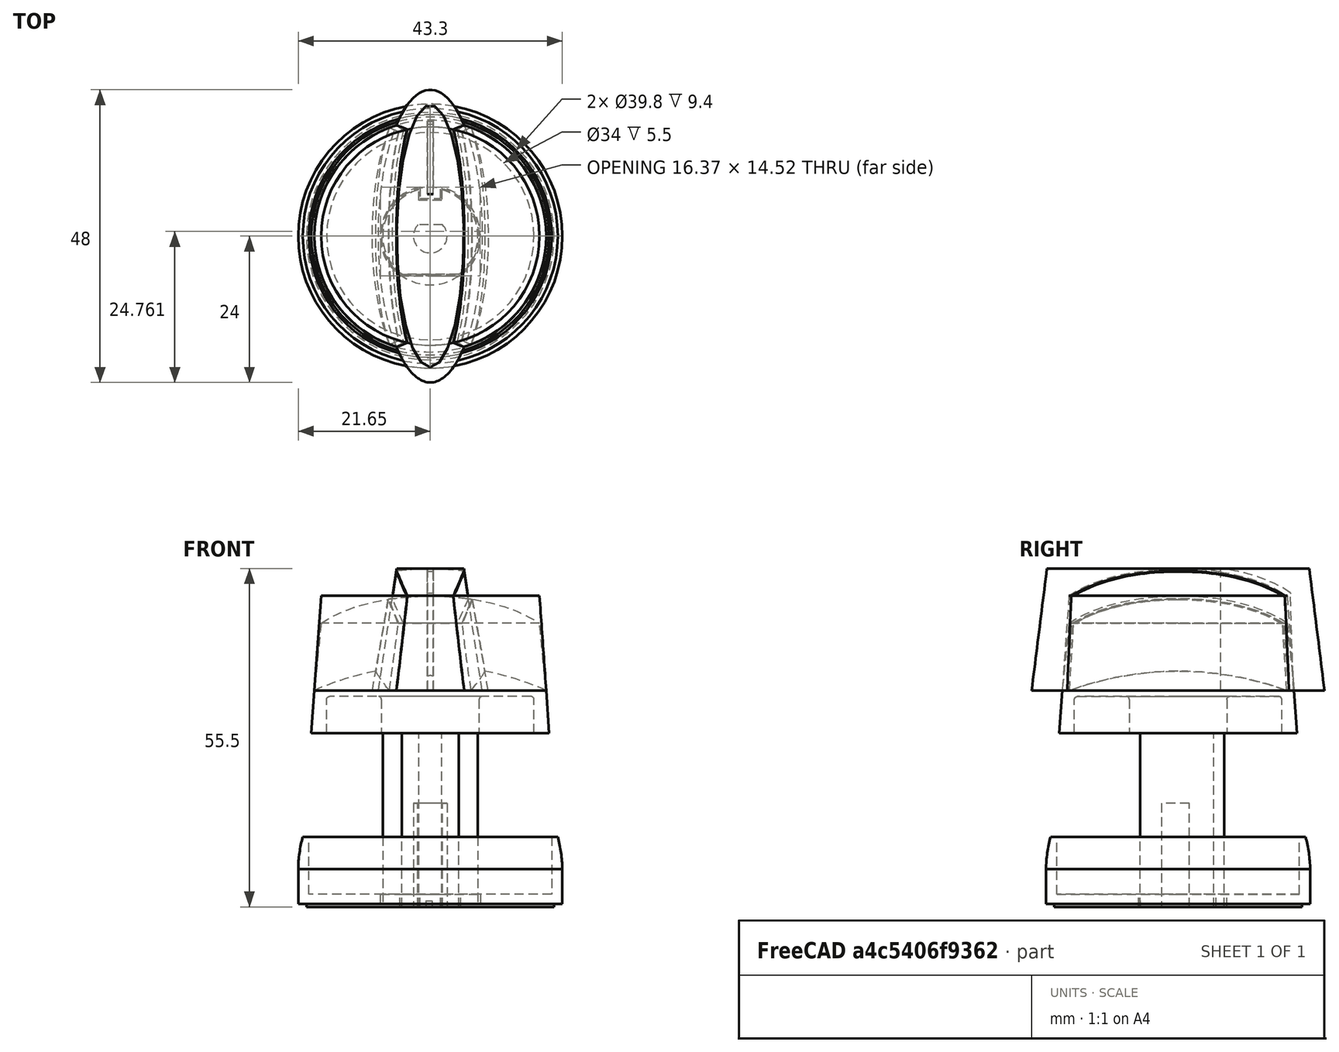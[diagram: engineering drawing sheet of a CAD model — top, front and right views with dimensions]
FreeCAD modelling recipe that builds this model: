
FCSTD DOCUMENT  (FreeCAD 0.18.4R)
Label: electrolux_ruchki_001
License: All rights reserved
LicenseURL: http://en.wikipedia.org/wiki/All_rights_reserved
objects: Sketcher::SketchObject×27, PartDesign::Body×9, PartDesign::Boolean×8, PartDesign::Fillet×8, PartDesign::AdditiveLoft×4, PartDesign::Pad×3, PartDesign::Pocket×3, PartDesign::Revolution×3, PartDesign::Plane×2, PartDesign::Groove×1, App::DocumentObjectGroup×1, PartDesign::AdditiveBox×1, Mesh::Feature×1
note: 84 computed .brp shape members not serialized (recipe doc carries the construction recipe); baked Part::Feature solids carry a one-line shape summary decoded from their .brp

FEATURE [Sketcher::SketchObject] Sketch
  sketch-geometry (8):
    g0: Circle CenterX=0 CenterY=0 CenterZ=0 NormalX=0 NormalY=0 NormalZ=1 AngleXU=0 Radius=21.65
    g1: ArcOfCircle CenterX=0 CenterY=0 CenterZ=0 NormalX=0 NormalY=0 NormalZ=1 AngleXU=0 Radius=8 StartAngle=5.37644 EndAngle=7.63345
    g2: LineSegment StartX=-1.75 StartY=6 StartZ=0 EndX=1.75 EndY=6 EndZ=0
    g3: LineSegment StartX=1.75 StartY=6 StartZ=0 EndX=1.75 EndY=7.80625 EndZ=0
    g4: LineSegment StartX=-1.75 StartY=7.80625 StartZ=0 EndX=-1.75 EndY=6 EndZ=0
    g5: GeomPoint X=0 Y=8 Z=0
    g6: LineSegment StartX=-4.93052 StartY=-6.3 StartZ=0 EndX=4.93052 EndY=-6.3 EndZ=0
    g7: ArcOfCircle CenterX=0 CenterY=0 CenterZ=0 NormalX=0 NormalY=0 NormalZ=1 AngleXU=0 Radius=8 StartAngle=1.79133 EndAngle=4.04833
  constraints (22):
    c: Coincident(g0,g-1)
    c: Radius(g0) = 21.65
    c: Coincident(g0,g1)
    c: Radius(g1) = 8
    c: Coincident(g2,g3)
    c: Coincident(g4,g2)
    c: Vertical(g3)
    c: Vertical(g4)
    c: PointOnObject(g5,g1)
    c: PointOnObject(g5,g-2)
    c: Horizontal(g6)
    c: DistanceY(g6,g2) = 12.3
    c: Coincident(g1,g6)
    c: Coincident(g7,g6)
    c: Coincident(g6,g7)
    c: Coincident(g7,g4)
    c: Coincident(g1,g7)
    c: Coincident(g1,g3)
    c: DistanceX(g2,g2) = 3.5
    c: Equal(g7,g1)
    c: Symmetric(g2,g2,g-2)
    c: DistanceY(g2,g5) = 2
FEATURE [Sketcher::SketchObject] CopySketch  label="основание"
  sketch-geometry (8):
    g0: Circle CenterX=0 CenterY=0 CenterZ=0 NormalX=0 NormalY=0 NormalZ=1 AngleXU=0 Radius=21.65
    g1: ArcOfCircle CenterX=0 CenterY=0 CenterZ=0 NormalX=0 NormalY=0 NormalZ=1 AngleXU=0 Radius=8.2 StartAngle=5.36799 EndAngle=7.64515
    g2: LineSegment StartX=-1.7 StartY=6.2 StartZ=0 EndX=1.7 EndY=6.2 EndZ=0
    g3: LineSegment StartX=1.7 StartY=6.2 StartZ=0 EndX=1.7 EndY=8.02185 EndZ=0
    g4: LineSegment StartX=-1.7 StartY=8.02185 StartZ=0 EndX=-1.7 EndY=6.2 EndZ=0
    g5: GeomPoint X=0 Y=8.2 Z=0
    g6: LineSegment StartX=-4.999 StartY=-6.5 StartZ=0 EndX=4.999 EndY=-6.5 EndZ=0
    g7: ArcOfCircle CenterX=0 CenterY=0 CenterZ=0 NormalX=0 NormalY=0 NormalZ=1 AngleXU=0 Radius=8.2 StartAngle=1.77963 EndAngle=4.05679
  constraints (22):
    c: Coincident(g0,g-1)
    c: Radius(g0) = 21.65
    c: Coincident(g0,g1)
    c: Radius(g1) = 8.2
    c: Coincident(g2,g3)
    c: Coincident(g4,g2)
    c: Vertical(g3)
    c: Vertical(g4)
    c: PointOnObject(g5,g1)
    c: PointOnObject(g5,g-2)
    c: Horizontal(g6)
    c: DistanceY(g6,g2) = 12.7
    c: Coincident(g1,g6)
    c: Coincident(g7,g6)
    c: Coincident(g6,g7)
    c: Coincident(g7,g4)
    c: Coincident(g1,g7)
    c: Coincident(g1,g3)
    c: DistanceX(g2,g2) = 3.4
    c: Equal(g7,g1)
    c: Symmetric(g2,g2,g-2)
    c: DistanceY(g2,g5) = 2
FEATURE [Sketcher::SketchObject] CopySketch001  label="карман2"
  Placement = pos=(0,0,0) rot=(1,0,0;3.14159rad)
  sketch-geometry (2):
    g0: Circle CenterX=0 CenterY=0 CenterZ=0 NormalX=0 NormalY=0 NormalZ=1 AngleXU=0 Radius=21.65
    g1: Circle CenterX=0 CenterY=0 CenterZ=0 NormalX=0 NormalY=0 NormalZ=1 AngleXU=0 Radius=20.3
  constraints (4):
    c: Radius(g1) = 20.3
    c: Radius(g0) = 21.65
    c: Coincident(g1,g-1)
    c: Coincident(g0,g1)
FEATURE [PartDesign::Pad] Pad
  Length = 11.5
  Length2 = 100
  Profile = -> CopySketch
  Type = 0
FEATURE [Sketcher::SketchObject] Sketch002  label="карман"
  MapMode = 5
  Placement = pos=(0,0,11.5) rot=(0,0,1;0rad)
  Support = -> [Pad]
  sketch-geometry (1):
    g0: Circle CenterX=0 CenterY=0 CenterZ=0 NormalX=0 NormalY=0 NormalZ=1 AngleXU=0 Radius=19.9
  constraints (2):
    c: Coincident(g0,g-1)
    c: Radius(g0) = 19.9
FEATURE [PartDesign::Pocket] Pocket
  BaseFeature = -> Pad
  Length = 9.4
  Length2 = 100
  Profile = -> Sketch002
  Type = 0
FEATURE [Sketcher::SketchObject] Sketch003
  MapMode = 5
  Placement = pos=(0,0,11.5) rot=(0,0,1;0rad)
  Support = -> [Pocket]
  sketch-geometry (1):
    g0: Circle CenterX=0 CenterY=0 CenterZ=0 NormalX=0 NormalY=0 NormalZ=1 AngleXU=0 Radius=20.5
  constraints (2):
    c: Coincident(g0,g-1)
    c: Radius(g0) = 20.5
FEATURE [PartDesign::Pocket] Pocket001
  BaseFeature = -> Pocket
  Length = 0.5
  Length2 = 100
  Profile = -> CopySketch001
  Type = 0
FEATURE [Sketcher::SketchObject] Sketch004  label="скругление"
  ExternalGeometry = -> [Pad]
  MapMode = 5
  Placement = pos=(0,0,0) rot=(1,0,0;1.5708rad)
  Support = -> [XZ_Plane]
  sketch-geometry (3):
    g0: LineSegment StartX=21.65 StartY=6.5 StartZ=0 EndX=21.65 EndY=11.5 EndZ=0
    g1: LineSegment StartX=20.9 StartY=11.5 StartZ=0 EndX=21.65 EndY=11.5 EndZ=0
    g2: ArcOfCircle CenterX=0 CenterY=5.80875 CenterZ=0 NormalX=0 NormalY=0 NormalZ=1 AngleXU=0 Radius=21.661 StartAngle=0.0319176 EndAngle=0.265862
  constraints (9):
    c: Coincident(g-3,g0)
    c: Horizontal(g1)
    c: Coincident(g1,g0)
    c: Coincident(g2,g1)
    c: PointOnObject(g2,g-2)
    c: DistanceX(g1,g0) = 0.75
    c: DistanceY(g2,g0) = 5
    c: Coincident(g0,g2)
    c: Vertical(g0)
FEATURE [Sketcher::SketchObject] CopySketch004
  Placement = pos=(0,0,0) rot=(1,0,0;1.5708rad)
  sketch-geometry (3):
    g0: LineSegment StartX=21.65 StartY=5.5 StartZ=0 EndX=21.65 EndY=11.5 EndZ=0
    g1: LineSegment StartX=20.9 StartY=11.5 StartZ=0 EndX=21.65 EndY=11.5 EndZ=0
    g2: ArcOfCircle CenterX=0 CenterY=5.84062 CenterZ=0 NormalX=0 NormalY=0 NormalZ=1 AngleXU=0 Radius=21.6527 StartAngle=6.26745 EndAngle=6.54763
  constraints (10):
    c: Horizontal(g1)
    c: Coincident(g1,g0)
    c: Coincident(g2,g1)
    c: PointOnObject(g2,g-2)
    c: DistanceX(g1,g0) = 0.75
    c: DistanceY(g2,g0) = 6
    c: Coincident(g0,g2)
    c: Vertical(g0)
    c: DistanceY(g-1,g0) = 11.5
    c: DistanceX(g-1,g0) = 21.65
FEATURE [PartDesign::Groove] Groove
  Angle = 360
  Axis = (0,2e-16,1)
  Base = (0,0,0)
  BaseFeature = -> Pocket001
  Profile = -> CopySketch004
  ReferenceAxis = -> CopySketch004 [V_Axis]
FEATURE [PartDesign::Body] Body  label="шайба_ручки"
  Group = -> [Pad,Sketch002,Pocket,Pocket001,Groove]
  Origin = -> Origin
  Tip = -> Groove
FEATURE [Sketcher::SketchObject] Sketch005
  MapMode = 5
  Support = -> [XY_Plane001]
  sketch-geometry (7):
    g0: ArcOfCircle CenterX=0 CenterY=0 CenterZ=0 NormalX=0 NormalY=0 NormalZ=1 AngleXU=0 Radius=7.8 StartAngle=5.35375 EndAngle=7.61452
    g1: LineSegment StartX=-1.85 StartY=5.85 StartZ=0 EndX=1.85 EndY=5.85 EndZ=0
    g2: LineSegment StartX=1.85 StartY=5.85 StartZ=0 EndX=1.85 EndY=7.57743 EndZ=0
    g3: LineSegment StartX=-1.85 StartY=7.57743 StartZ=0 EndX=-1.85 EndY=5.85 EndZ=0
    g4: GeomPoint X=0 Y=7.8 Z=0
    g5: LineSegment StartX=-4.66664 StartY=-6.25 StartZ=0 EndX=4.66664 EndY=-6.25 EndZ=0
    g6: ArcOfCircle CenterX=0 CenterY=0 CenterZ=0 NormalX=0 NormalY=0 NormalZ=1 AngleXU=0 Radius=7.8 StartAngle=1.81026 EndAngle=4.07103
  constraints (19):
    c: Coincident(g1,g2)
    c: Coincident(g3,g1)
    c: Vertical(g2)
    c: Vertical(g3)
    c: PointOnObject(g4,g0)
    c: PointOnObject(g4,g-2)
    c: Coincident(g0,g5)
    c: Coincident(g6,g5)
    c: Coincident(g5,g6)
    c: Coincident(g6,g3)
    c: Symmetric(g1,g1,g-2)
    c: DistanceX(g1,g1) = 3.7
    c: DistanceY(g1,g4) = 1.95
    c: DistanceY(g5,g1) = 12.1
    c: Symmetric(g5,g0,g-2)
    c: Coincident(g0,g-1)
    c: Coincident(g2,g0)
    c: Coincident(g0,g6)
    c: Diameter(g0) = 15.6
FEATURE [PartDesign::Pad] Pad001
  Length = 31
  Length2 = 100
  Profile = -> Sketch005
  Type = 0
FEATURE [Sketcher::SketchObject] Sketch006
  MapMode = 5
  Support = -> [XY_Plane001]
  sketch-geometry (3):
    g0: ArcOfCircle CenterX=0 CenterY=0 CenterZ=0 NormalX=0 NormalY=0 NormalZ=1 AngleXU=0 Radius=2.5 StartAngle=2.2143 EndAngle=7.21048
    g1: LineSegment StartX=-1.5 StartY=2 StartZ=0 EndX=1.5 EndY=2 EndZ=0
    g2: GeomPoint X=0 Y=-2.5 Z=0
  constraints (9):
    c: Coincident(g0,g-1)
    c: Radius(g0) = 2.5
    c: PointOnObject(g2,g-2)
    c: PointOnObject(g2,g0)
    c: Coincident(g0,g1)
    c: Coincident(g0,g1)
    c: DistanceY(g2,g0) = 4.5
    c: Symmetric(g0,g0,g-2)
    c: Coincident(g1,g0)
FEATURE [Sketcher::SketchObject] CopyCopySketch006  label="выемка_под_вал"
  Placement = pos=(0,0,0) rot=(0,1,0;3.14159rad)
  sketch-geometry (3):
    g0: ArcOfCircle CenterX=0 CenterY=0 CenterZ=0 NormalX=0 NormalY=0 NormalZ=1 AngleXU=0 Radius=2.75 StartAngle=2.4037 EndAngle=7.02107
    g1: LineSegment StartX=-2.0347 StartY=1.85 StartZ=0 EndX=2.0347 EndY=1.85 EndZ=0
    g2: GeomPoint X=0 Y=-2.75 Z=0
  constraints (9):
    c: Coincident(g0,g-1)
    c: PointOnObject(g2,g-2)
    c: PointOnObject(g2,g0)
    c: Coincident(g0,g1)
    c: Coincident(g0,g1)
    c: DistanceY(g2,g0) = 4.6
    c: Symmetric(g0,g0,g-2)
    c: Coincident(g1,g0)
    c: Diameter(g0) = 5.5
FEATURE [PartDesign::Pocket] Pocket002
  BaseFeature = -> Pad001
  Length = 17
  Length2 = 100
  Profile = -> CopyCopySketch006
  Type = 0
FEATURE [Sketcher::SketchObject] Sketch008
  MapMode = 5
  Placement = pos=(0,0,28.5) rot=(1,0,0;3.14159rad)
  sketch-geometry (2):
    g0: Circle CenterX=0 CenterY=0 CenterZ=0 NormalX=0 NormalY=0 NormalZ=1 AngleXU=0 Radius=17
    g1: Circle CenterX=0 CenterY=0 CenterZ=0 NormalX=0 NormalY=0 NormalZ=1 AngleXU=0 Radius=8
  constraints (4):
    c: Coincident(g0,g-1)
    c: Diameter(g0) = 34
    c: Coincident(g1,g0)
    c: Diameter(g1) = 16
FEATURE [Sketcher::SketchObject] Sketch012
  ExternalGeometry = -> [Sketch008]
  MapMode = 5
  Placement = pos=(0,0,0) rot=(1,0,0;1.5708rad)
  Support = -> [XZ_Plane001]
  sketch-geometry (9):
    g0: LineSegment StartX=19.5 StartY=28.5 StartZ=0 EndX=19 EndY=35.5 EndZ=0
    g1: LineSegment StartX=19.5 StartY=28.5 StartZ=0 EndX=17 EndY=28.5 EndZ=0
    g2: LineSegment StartX=17 StartY=28.5 StartZ=0 EndX=17 EndY=34.5 EndZ=0
    g3: LineSegment StartX=17 StartY=34.5 StartZ=0 EndX=8 EndY=34.5 EndZ=0
    g4: LineSegment StartX=8 StartY=34.5 StartZ=0 EndX=8 EndY=28.5 EndZ=0
    g5: LineSegment StartX=8 StartY=28.5 StartZ=0 EndX=0 EndY=28.5 EndZ=0
    g6: LineSegment StartX=0 StartY=28.5 StartZ=0 EndX=2.9e-15 EndY=39.5 EndZ=0
    g7: ArcOfCircle CenterX=0 CenterY=-7.625 CenterZ=0 NormalX=0 NormalY=0 NormalZ=1 AngleXU=0 Radius=47.125 StartAngle=1.1558 EndAngle=1.5708
    g8: LineSegment [constr] StartX=19.5 StartY=28.5 StartZ=0 EndX=17.8929 EndY=51 EndZ=0
  constraints (27):
    c: Coincident(g1,g0)
    c: Coincident(g2,g1)
    c: Horizontal(g3)
    c: Coincident(g4,g3)
    c: Coincident(g5,g4)
    c: Coincident(g6,g5)
    c: PointOnObject(g5,g-2)
    c: Coincident(g3,g2)
    c: Coincident(g0,g7)
    c: Coincident(g7,g6)
    c: Horizontal(g5)
    c: Vertical(g4)
    c: Vertical(g2)
    c: PointOnObject(g7,g-2)
    c: DistanceY(g1,g2) = 6
    c: DistanceY(g5,g6) = 11
    c: DistanceY(g0,g0) = 7
    c: DistanceX(g0,g0) = 0.5
    c: PointOnObject(g6,g-2)
    c: Horizontal(g1)
    c: DistanceX(g5,g4) = 8
    c: Coincident(g-3,g1)
    c: DistanceY(g0,g5) = 0
    c: DistanceX(g5,g0) = 19.5
    c: Coincident(g0,g8)
    c: PointOnObject(g0,g8)
    c: DistanceY(g0,g8) = 22.5
FEATURE [Sketcher::SketchObject] Sketch007
  AttachmentOffset = pos=(0,0,28.5) rot=(0,0,1;0rad)
  ExternalGeometry = -> [Sketch012]
  MapMode = 5
  Placement = pos=(0,0,28.5) rot=(0,0,1;0rad)
  Support = -> [XY_Plane001]
  sketch-geometry (1):
    g0: Circle CenterX=9e-16 CenterY=0 CenterZ=0 NormalX=0 NormalY=0 NormalZ=1 AngleXU=0 Radius=19.5
  constraints (2):
    c: Coincident(g0,g-1)
    c: PointOnObject(g-3,g0)
FEATURE [Sketcher::SketchObject] Sketch011
  AttachmentOffset = pos=(0,0,35.5) rot=(0,0,1;0rad)
  ExternalGeometry = -> [Sketch012]
  MapMode = 5
  Placement = pos=(0,0,35.5) rot=(0,0,1;0rad)
  Support = -> [XY_Plane001]
  sketch-geometry (1):
    g0: Circle CenterX=0 CenterY=0 CenterZ=0 NormalX=0 NormalY=0 NormalZ=1 AngleXU=0 Radius=19
  constraints (2):
    c: Coincident(g0,g-1)
    c: PointOnObject(g-3,g0)
FEATURE [PartDesign::Plane] DatumPlane
  Length = 46.8
  MapMode = 5
  Placement = pos=(0,6e-15,28.5) rot=(1,0,0;3.14159rad)
  ResizeMode = 0
  Width = 46.8
FEATURE [Sketcher::SketchObject] Sketch013
  AttachmentOffset = pos=(0,0,-7) rot=(0,0,1;0rad)
  MapMode = 5
  Placement = pos=(0,6e-15,35.5) rot=(1,0,0;3.14159rad)
  Support = -> [DatumPlane]
  sketch-geometry (5):
    g0: Ellipse CenterX=0 CenterY=0 CenterZ=0 NormalX=0 NormalY=0 NormalZ=1 MajorRadius=25 MinorRadius=9.5 AngleXU=1.5708
    g1: LineSegment [constr] StartX=0 StartY=25 StartZ=0 EndX=0 EndY=-25 EndZ=0
    g2: LineSegment [constr] StartX=-9.5 StartY=0 StartZ=0 EndX=9.5 EndY=0 EndZ=0
    g3: GeomPoint X=0 Y=23.1247 Z=0
    g4: GeomPoint X=0 Y=-23.1247 Z=0
  constraints (5):
    c: InternalAlignment(g1-g4 -> g0) x4
    c: Coincident(g0,g-1)
    c: PointOnObject(g3,g-2)
    c: DistanceX(g2,g2) = 19
    c: DistanceY(g1,g1) = 50
FEATURE [Sketcher::SketchObject] Sketch014
  AttachmentOffset = pos=(0,0,51) rot=(0,0,1;0rad)
  MapMode = 5
  Placement = pos=(0,0,51) rot=(0,0,1;0rad)
  Support = -> [XY_Plane001]
  sketch-geometry (1):
    g0: Circle CenterX=0 CenterY=0 CenterZ=0 NormalX=0 NormalY=0 NormalZ=1 AngleXU=0 Radius=17.8929
  constraints (1):
    c: Coincident(g0,g-1)
FEATURE [PartDesign::Revolution] Revolution
  Angle = 360
  Axis = (0,-2e-16,1)
  Base = (0,0,0)
  BaseFeature = -> Pocket002
  Profile = -> Sketch012
  ReferenceAxis = -> Sketch012 [V_Axis]
  Reversed = true
FEATURE [Sketcher::SketchObject] Sketch015
  AttachmentOffset = pos=(0,0,-27) rot=(0,0,1;0rad)
  MapMode = 5
  Placement = pos=(0,6e-15,55.5) rot=(1,0,0;3.14159rad)
  Support = -> [DatumPlane]
  sketch-geometry (5):
    g0: Ellipse CenterX=0 CenterY=0 CenterZ=0 NormalX=0 NormalY=0 NormalZ=1 MajorRadius=22.5 MinorRadius=6 AngleXU=1.5708
    g1: LineSegment [constr] StartX=0 StartY=22.5 StartZ=0 EndX=0 EndY=-22.5 EndZ=0
    g2: LineSegment [constr] StartX=-6 StartY=0 StartZ=0 EndX=6 EndY=0 EndZ=0
    g3: GeomPoint X=0 Y=21.6852 Z=0
    g4: GeomPoint X=0 Y=-21.6852 Z=0
  constraints (5):
    c: InternalAlignment(g1-g4 -> g0) x4
    c: Coincident(g0,g-1)
    c: PointOnObject(g3,g-2)
    c: DistanceX(g2,g2) = 12
    c: DistanceY(g1,g1) = 45
FEATURE [Sketcher::SketchObject] Sketch016
  MapMode = 5
  Placement = pos=(0,0,0) rot=(1,0,0;1.5708rad)
  Support = -> [XZ_Plane001]
  sketch-geometry (8):
    g0: LineSegment StartX=0 StartY=55.5 StartZ=0 EndX=0 EndY=51 EndZ=0
    g1: LineSegment StartX=0 StartY=51 StartZ=0 EndX=17.8929 EndY=51 EndZ=0
    g2: Circle [constr] CenterX=0 CenterY=55.5 CenterZ=0 NormalX=0 NormalY=0 NormalZ=1 AngleXU=0 Radius=1
    g3: Circle [constr] CenterX=11.43 CenterY=55.32 CenterZ=0 NormalX=0 NormalY=0 NormalZ=1 AngleXU=0 Radius=1
    g4: Circle [constr] CenterX=17.8929 CenterY=51 CenterZ=0 NormalX=0 NormalY=0 NormalZ=1 AngleXU=0 Radius=1
    g5: BSplineCurve PolesCount=3 KnotsCount=2 Degree=2 IsPeriodic=0
    g6: GeomPoint [constr] X=0 Y=55.5 Z=0
    g7: GeomPoint [constr] X=17.8929 Y=51 Z=0
  constraints (17):
    c: Coincident(g1,g0)
    c: Radius(g2) = 1
    c: Equal(g2,g3)
    c: Equal(g2,g4)
    c: Coincident(g5,g1)
    c: InternalAlignment(g2,g5)
    c: InternalAlignment(g3,g5)
    c: InternalAlignment(g4,g5)
    c: InternalAlignment(g6,g5)
    c: InternalAlignment(g7,g5)
    c: Coincident(g5,g0)
    c: Horizontal(g1)
    c: Vertical(g0)
    c: PointOnObject(g0,g-2)
    c: DistanceY(g0,g0) = 4.5
    c: DistanceX(g0,g3) = 11.43
    c: DistanceY(g1,g3) = 4.32
FEATURE [App::DocumentObjectGroup] Construction
  Group = -> [Sketch,Sketch003,Sketch004,Sketch006,Sketch016,Sketch013,Sketch011]
FEATURE [Sketcher::SketchObject] CopySketch011
  Placement = pos=(0,0,35.5) rot=(0,0,1;0rad)
  sketch-geometry (1):
    g0: Circle CenterX=0 CenterY=0 CenterZ=0 NormalX=0 NormalY=0 NormalZ=1 AngleXU=0 Radius=19
  constraints (1):
    c: Coincident(g0,g-1)
FEATURE [PartDesign::AdditiveLoft] AdditiveLoft
  Closed = false
  Placement = pos=(0,0,35.5) rot=(0,0,1;0rad)
  Profile = -> CopySketch011
  Ruled = false
  Sections = -> [Sketch014]
FEATURE [PartDesign::Body] Body002
  Group = -> [AdditiveLoft]
  Origin = -> Origin002
  Tip = -> AdditiveLoft
FEATURE [Sketcher::SketchObject] CopySketch013
  Placement = pos=(0,6e-15,35.5) rot=(1,0,0;3.14159rad)
  sketch-geometry (5):
    g0: Ellipse CenterX=0 CenterY=0 CenterZ=0 NormalX=0 NormalY=0 NormalZ=1 MajorRadius=25 MinorRadius=9.5 AngleXU=1.5708
    g1: LineSegment [constr] StartX=0 StartY=25 StartZ=0 EndX=0 EndY=-25 EndZ=0
    g2: LineSegment [constr] StartX=-9.5 StartY=0 StartZ=0 EndX=9.5 EndY=0 EndZ=0
    g3: GeomPoint X=2.6e-15 Y=23.1247 Z=0
    g4: GeomPoint X=0 Y=-23.1247 Z=0
  constraints (5):
    c: InternalAlignment(g1-g4 -> g0) x4
    c: Coincident(g0,g-1)
    c: PointOnObject(g3,g-2)
    c: DistanceX(g2,g2) = 19
    c: DistanceY(g1,g1) = 50
FEATURE [PartDesign::AdditiveLoft] AdditiveLoft001
  Closed = false
  Placement = pos=(0,6e-15,35.5) rot=(1,0,0;3.14159rad)
  Profile = -> CopySketch013
  Ruled = false
  Sections = -> [Sketch015]
FEATURE [Sketcher::SketchObject] CopySketch016
  Placement = pos=(0,0,0) rot=(1,0,0;1.5708rad)
  sketch-geometry (8):
    g0: LineSegment StartX=0 StartY=55.5 StartZ=0 EndX=0 EndY=51 EndZ=0
    g1: LineSegment StartX=0 StartY=51 StartZ=0 EndX=17.8929 EndY=51 EndZ=0
    g2: Circle [constr] CenterX=0 CenterY=55.5 CenterZ=0 NormalX=0 NormalY=0 NormalZ=1 AngleXU=0 Radius=1
    g3: Circle [constr] CenterX=11.43 CenterY=55.32 CenterZ=0 NormalX=0 NormalY=0 NormalZ=1 AngleXU=0 Radius=1
    g4: Circle [constr] CenterX=17.8929 CenterY=51 CenterZ=0 NormalX=0 NormalY=0 NormalZ=1 AngleXU=0 Radius=1
    g5: BSplineCurve PolesCount=3 KnotsCount=2 Degree=2 IsPeriodic=0
    g6: GeomPoint [constr] X=0 Y=55.5 Z=0
    g7: GeomPoint [constr] X=17.8929 Y=51 Z=0
  constraints (17):
    c: Coincident(g1,g0)
    c: Radius(g2) = 1
    c: Equal(g2,g3)
    c: Equal(g2,g4)
    c: Coincident(g5,g1)
    c: InternalAlignment(g2,g5)
    c: InternalAlignment(g3,g5)
    c: InternalAlignment(g4,g5)
    c: InternalAlignment(g6,g5)
    c: InternalAlignment(g7,g5)
    c: Coincident(g5,g0)
    c: Horizontal(g1)
    c: Vertical(g0)
    c: PointOnObject(g0,g-2)
    c: DistanceY(g0,g0) = 4.5
    c: DistanceX(g0,g3) = 11.43
    c: DistanceY(g1,g3) = 4.32
FEATURE [PartDesign::Revolution] Revolution001
  Angle = 360
  Axis = (0,-2e-16,1)
  Base = (0,0,0)
  Placement = pos=(0,0,0) rot=(1,0,0;1.5708rad)
  Profile = -> CopySketch016
  ReferenceAxis = -> CopySketch016 [V_Axis]
  Reversed = true
FEATURE [Sketcher::SketchObject] Sketch017
  MapMode = 5
  Placement = pos=(0,0,0) rot=(0.57735,0.57735,0.57735;2.0944rad)
  Support = -> [YZ_Plane005]
  sketch-geometry (9):
    g0: LineSegment StartX=18.9 StartY=35.5 StartZ=0 EndX=18.4 EndY=51.5 EndZ=0
    g1: Circle [constr] CenterX=18.4 CenterY=51.5 CenterZ=0 NormalX=0 NormalY=0 NormalZ=1 AngleXU=0 Radius=0.9
    g2: Circle [constr] CenterX=13.9 CenterY=54.6 CenterZ=0 NormalX=0 NormalY=0 NormalZ=1 AngleXU=0 Radius=0.9
    g3: Circle [constr] CenterX=6.9 CenterY=55.5 CenterZ=0 NormalX=0 NormalY=0 NormalZ=1 AngleXU=0 Radius=0.9
    g4: BSplineCurve PolesCount=3 KnotsCount=2 Degree=2 IsPeriodic=0
    g5: GeomPoint [constr] X=18.4 Y=51.5 Z=0
    g6: GeomPoint [constr] X=6.9 Y=55.5 Z=0
    g7: LineSegment StartX=6.9 StartY=55.5 StartZ=0 EndX=6.9 EndY=35.5 EndZ=0
    g8: LineSegment StartX=6.9 StartY=35.5 StartZ=0 EndX=18.9 EndY=35.5 EndZ=0
  constraints (22):
    c: Coincident(g4,g0)
    c: Radius(g1) = 0.9
    c: Equal(g1,g2)
    c: Equal(g1,g3)
    c: InternalAlignment(g1,g4)
    c: InternalAlignment(g2,g4)
    c: InternalAlignment(g3,g4)
    c: InternalAlignment(g5,g4)
    c: InternalAlignment(g6,g4)
    c: Coincident(g7,g4)
    c: Vertical(g7)
    c: Coincident(g8,g7)
    c: Coincident(g8,g0)
    c: Horizontal(g8)
    c: DistanceX(g0,g0) = 0.5
    c: DistanceY(g0,g0) = 16
    c: DistanceX(g-1,g7) = 6.9
    c: DistanceY(g-1,g4) = 55.5
    c: DistanceX(g7,g0) = 12
    c: DistanceY(g7,g4) = 20
    c: DistanceX(g4,g2) = 7
    c: DistanceY(g2,g4) = 0.9
FEATURE [PartDesign::Pad] Pad002
  Length = 1
  Length2 = 100
  Midplane = true
  Placement = pos=(0,0,0) rot=(0.57735,0.57735,0.57735;2.0944rad)
  Profile = -> Sketch017
  Type = 0
FEATURE [PartDesign::Body] Body005
  Group = -> [Sketch017,Pad002]
  Origin = -> Origin005
  Tip = -> Pad002
FEATURE [Sketcher::SketchObject] CopySketch017
  Placement = pos=(0,6e-15,35.5) rot=(1,0,0;3.14159rad)
  sketch-geometry (5):
    g0: Ellipse CenterX=0 CenterY=0 CenterZ=0 NormalX=0 NormalY=0 NormalZ=1 MajorRadius=24 MinorRadius=8.5 AngleXU=1.5708
    g1: LineSegment [constr] StartX=0 StartY=24 StartZ=0 EndX=0 EndY=-24 EndZ=0
    g2: LineSegment [constr] StartX=-8.5 StartY=0 StartZ=0 EndX=8.5 EndY=0 EndZ=0
    g3: GeomPoint X=0 Y=22.4444 Z=0
    g4: GeomPoint X=0 Y=-22.4444 Z=0
  constraints (5):
    c: InternalAlignment(g1-g4 -> g0) x4
    c: Coincident(g0,g-1)
    c: PointOnObject(g3,g-2)
    c: DistanceX(g2,g2) = 17
    c: DistanceY(g1,g1) = 48
FEATURE [PartDesign::Plane] DatumPlane001
  Length = 24
  MapMode = 5
  Placement = pos=(0,6e-15,28.5) rot=(1,0,0;3.14159rad)
  ResizeMode = 0
  Width = 24
FEATURE [Sketcher::SketchObject] Sketch018
  AttachmentOffset = pos=(0,0,-27) rot=(0,0,1;0rad)
  MapMode = 5
  Placement = pos=(0,6e-15,55.5) rot=(1,0,0;3.14159rad)
  Support = -> [DatumPlane001]
  sketch-geometry (5):
    g0: Ellipse CenterX=0 CenterY=0 CenterZ=0 NormalX=0 NormalY=0 NormalZ=1 MajorRadius=21.5 MinorRadius=5.5 AngleXU=1.5708
    g1: LineSegment [constr] StartX=0 StartY=21.5 StartZ=0 EndX=0 EndY=-21.5 EndZ=0
    g2: LineSegment [constr] StartX=-5.5 StartY=0 StartZ=0 EndX=5.5 EndY=0 EndZ=0
    g3: GeomPoint X=0 Y=20.7846 Z=0
    g4: GeomPoint X=0 Y=-20.7846 Z=0
  constraints (5):
    c: InternalAlignment(g1-g4 -> g0) x4
    c: Coincident(g0,g-1)
    c: PointOnObject(g3,g-2)
    c: DistanceX(g2,g2) = 11
    c: DistanceY(g1,g1) = 43
FEATURE [PartDesign::AdditiveLoft] AdditiveLoft002
  Closed = false
  Placement = pos=(0,6e-15,35.5) rot=(1,0,0;3.14159rad)
  Profile = -> CopySketch017
  Ruled = false
  Sections = -> [Sketch018]
FEATURE [PartDesign::Body] Body006
  Group = -> [AdditiveLoft002]
  Origin = -> Origin006
  Tip = -> AdditiveLoft002
FEATURE [Sketcher::SketchObject] CopySketch018
  Placement = pos=(0,0,0) rot=(1,0,0;1.5708rad)
  sketch-geometry (8):
    g0: LineSegment StartX=0 StartY=51 StartZ=0 EndX=0 EndY=46.5 EndZ=0
    g1: LineSegment StartX=0 StartY=46.5 StartZ=0 EndX=17.89 EndY=46.5 EndZ=0
    g2: Circle [constr] CenterX=0 CenterY=51 CenterZ=0 NormalX=0 NormalY=0 NormalZ=1 AngleXU=0 Radius=1
    g3: Circle [constr] CenterX=11.43 CenterY=50.82 CenterZ=0 NormalX=0 NormalY=0 NormalZ=1 AngleXU=0 Radius=1
    g4: Circle [constr] CenterX=17.89 CenterY=46.5 CenterZ=0 NormalX=0 NormalY=0 NormalZ=1 AngleXU=0 Radius=1
    g5: BSplineCurve PolesCount=3 KnotsCount=2 Degree=2 IsPeriodic=0
    g6: GeomPoint [constr] X=0 Y=51 Z=0
    g7: GeomPoint [constr] X=17.89 Y=46.5 Z=0
  constraints (19):
    c: Coincident(g1,g0)
    c: Radius(g2) = 1
    c: Equal(g2,g3)
    c: Equal(g2,g4)
    c: Coincident(g5,g1)
    c: InternalAlignment(g2,g5)
    c: InternalAlignment(g3,g5)
    c: InternalAlignment(g4,g5)
    c: InternalAlignment(g6,g5)
    c: InternalAlignment(g7,g5)
    c: Coincident(g5,g0)
    c: Horizontal(g1)
    c: Vertical(g0)
    c: PointOnObject(g0,g-2)
    c: DistanceY(g0,g0) = 4.5
    c: DistanceX(g0,g3) = 11.43
    c: DistanceY(g1,g3) = 4.32
    c: DistanceY(g-1,g0) = 46.5
    c: DistanceX(g0,g1) = 17.89
FEATURE [PartDesign::Revolution] Revolution002
  Angle = 360
  Axis = (0,2e-16,1)
  Base = (0,0,0)
  Placement = pos=(0,0,0) rot=(1,0,0;1.5708rad)
  Profile = -> CopySketch018
  ReferenceAxis = -> CopySketch018 [V_Axis]
  Reversed = true
FEATURE [Sketcher::SketchObject] Sketch019
  AttachmentOffset = pos=(0,0,46.5) rot=(0,0,1;0rad)
  MapMode = 5
  Placement = pos=(0,0,46.5) rot=(0,0,1;0rad)
  Support = -> [XY_Plane008]
  sketch-geometry (1):
    g0: Circle CenterX=0 CenterY=0 CenterZ=0 NormalX=0 NormalY=0 NormalZ=1 AngleXU=0 Radius=17.8929
  constraints (1):
    c: Coincident(g0,g-1)
FEATURE [Sketcher::SketchObject] CopySketch019
  Placement = pos=(0,0,35.5) rot=(0,0,1;0rad)
  sketch-geometry (1):
    g0: Circle CenterX=0 CenterY=0 CenterZ=0 NormalX=0 NormalY=0 NormalZ=1 AngleXU=0 Radius=19
  constraints (1):
    c: Coincident(g0,g-1)
FEATURE [PartDesign::AdditiveLoft] AdditiveLoft003
  Closed = false
  Placement = pos=(0,0,35.5) rot=(0,0,1;0rad)
  Profile = -> CopySketch019
  Ruled = false
  Sections = -> [Sketch019]
FEATURE [PartDesign::Body] Body008
  Group = -> [AdditiveLoft003]
  Origin = -> Origin008
  Tip = -> AdditiveLoft003
FEATURE [PartDesign::Boolean] Boolean
  BaseFeature = -> Revolution002
  Group = -> [Body008]
  Type = 0
FEATURE [PartDesign::Body] Body007
  Group = -> [Revolution002,Boolean]
  Origin = -> Origin007
  Tip = -> Boolean
FEATURE [PartDesign::Boolean] Boolean001
  BaseFeature = -> Revolution001
  Group = -> [Body002]
  Type = 0
FEATURE [PartDesign::Boolean] Boolean002
  BaseFeature = -> Boolean001
  Group = -> [Body006]
  Type = 2
FEATURE [PartDesign::Boolean] Boolean003
  BaseFeature = -> AdditiveLoft001
  Group = -> [Body007]
  Type = 2
FEATURE [PartDesign::Body] Body004
  Group = -> [AdditiveLoft001,Boolean003]
  Origin = -> Origin004
  Tip = -> Boolean003
FEATURE [PartDesign::Boolean] Boolean004
  BaseFeature = -> Boolean002
  Group = -> [Body004]
  Type = 0
FEATURE [PartDesign::Boolean] Boolean005
  BaseFeature = -> Boolean004
  Group = -> [Body005]
  Type = 0
FEATURE [PartDesign::Body] Body003
  Group = -> [Revolution001,Boolean001,Boolean002,Boolean004,Boolean005]
  Origin = -> Origin003
  Tip = -> Boolean005
FEATURE [PartDesign::Boolean] Boolean006
  BaseFeature = -> Revolution
  Group = -> [Body003]
  Type = 0
FEATURE [PartDesign::Fillet] Fillet
  Base = -> Boolean006 [Edge28]
  BaseFeature = -> Boolean006
  Radius = 0.5
FEATURE [PartDesign::Fillet] Fillet001
  Base = -> Fillet [Edge2]
  BaseFeature = -> Fillet
  Radius = 0.5
FEATURE [PartDesign::Fillet] Fillet002
  Base = -> Fillet001 [Edge83]
  BaseFeature = -> Fillet001
  Radius = 0.2
FEATURE [PartDesign::Fillet] Fillet003
  Base = -> Fillet002 [Edge25,Edge32]
  BaseFeature = -> Fillet002
  Radius = 0.2
FEATURE [PartDesign::Fillet] Fillet004
  Base = -> Fillet003 [Edge54]
  BaseFeature = -> Fillet003
  Radius = 0.1
FEATURE [PartDesign::Fillet] Fillet005
  Base = -> Fillet004 [Edge22]
  BaseFeature = -> Fillet004
  Radius = 0.1
FEATURE [PartDesign::Fillet] Fillet006
  Base = -> Fillet005 [Edge85]
  BaseFeature = -> Fillet005
  Radius = 0.1
FEATURE [PartDesign::Fillet] Fillet007
  Base = -> Fillet006 [Edge88,Edge86]
  BaseFeature = -> Fillet006
  Radius = 0.1
FEATURE [PartDesign::AdditiveBox] Box
  AttacherType = Attacher::AttachEngine3D
  AttachmentOffset = pos=(1,0,12.2) rot=(0,0,1;0rad)
  BaseFeature = -> Fillet007
  Height = 1
  Length = 1
  MapMode = 6
  Placement = pos=(-0.7,-6,2.7e-15) rot=(1,0,0;1.5708rad)
  Support = -> [Groove,Fillet007]
  Width = 1
FEATURE [PartDesign::Boolean] Boolean007
  BaseFeature = -> Box
  Group = -> [Body]
  Type = 0
FEATURE [PartDesign::Body] Body001  label="ручка"
  Group = -> [Sketch005,Pad001,Pocket002,Sketch007,Sketch008,Sketch012,DatumPlane,Revolution,Boolean006,Fillet,Fillet001,Fillet002,Fillet003,Fillet004,Fillet005,Fillet006,Fillet007,Box,Boolean007]
  Origin = -> Origin001
  Tip = -> Boolean007
FEATURE [Mesh::Feature] Mesh  label="ручка (Meshed)"
